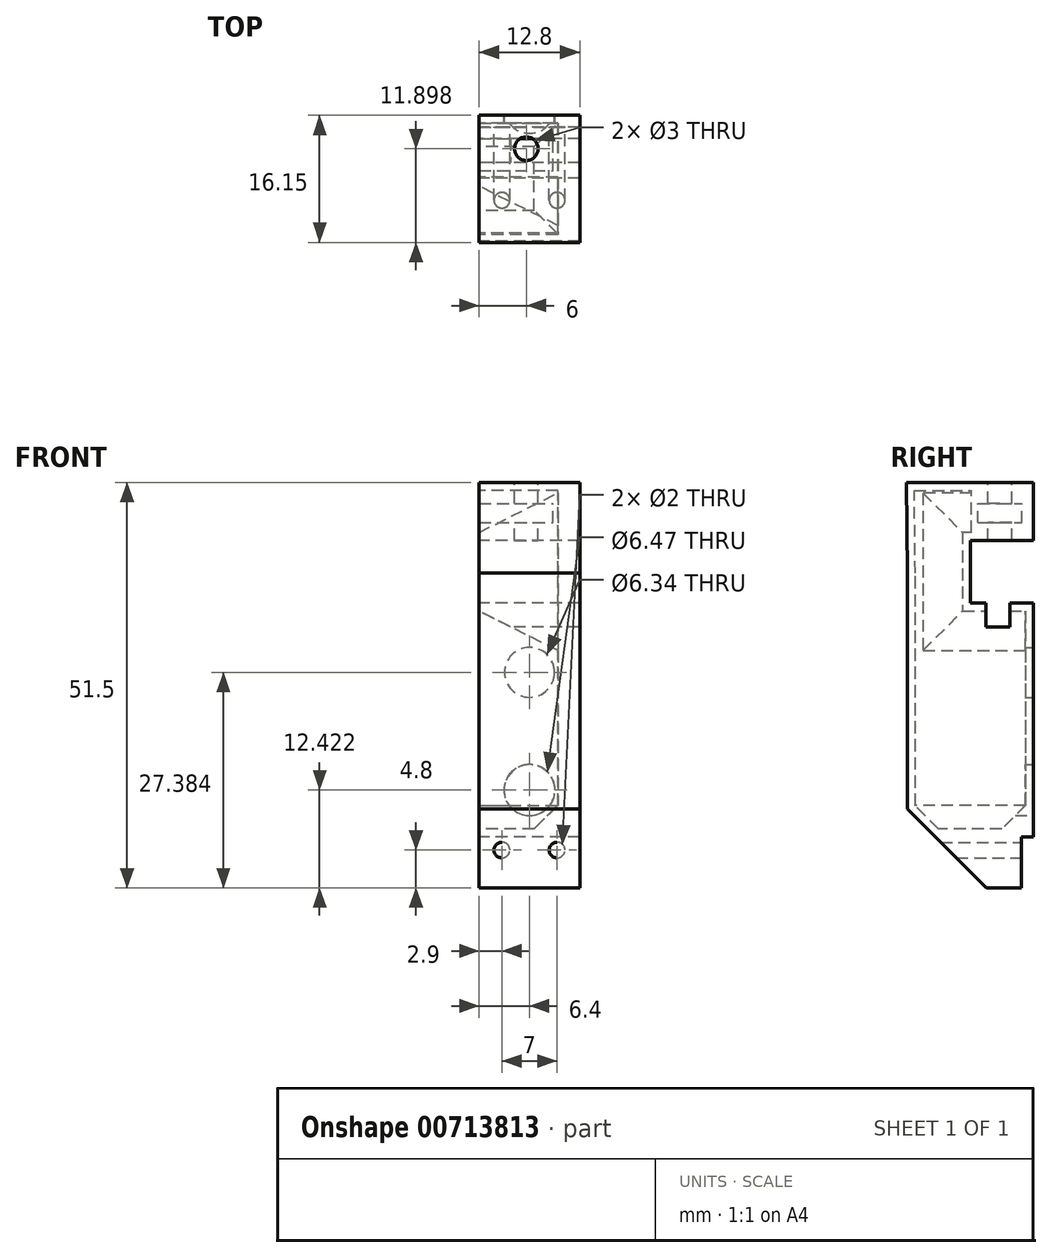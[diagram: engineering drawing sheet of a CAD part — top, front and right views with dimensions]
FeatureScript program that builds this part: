
annotation { "Feature Type Name" : "Feature", "Feature Type Description" : "" }
export const myFeature = defineFeature(function(context is Context, id is Id, definition is map)
    precondition{}
    {
        {
            var Q0;
            Q0=qCreatedBy(makeId("Right.planeOp"),FACE);
            var sketch = newSketch(context, id + "F0", { "sketchPlane" : qUnion([Q0])});
            skLineSegment(sketch, "E0.bottom", {"start": v(0, 4.16) * mm, "end": v(-8, 4.16) * mm});
            skLineSegment(sketch, "E0.top", {"start": v(0, -3.84) * mm, "end": v(-8, -3.84) * mm});
            skLineSegment(sketch, "E0.left", {"start": v(0, 4.16) * mm, "end": v(0, -3.84) * mm});
            skLineSegment(sketch, "E0.right", {"start": v(-8, 4.16) * mm, "end": v(-8, -3.84) * mm});
            skLineSegment(sketch, "E1.bottom", {"start": v(-16, 0) * mm, "end": v(0, 0) * mm});
            skLineSegment(sketch, "E1.top", {"start": v(-16, -40) * mm, "end": v(0, -40) * mm});
            skLineSegment(sketch, "E1.left", {"start": v(-16, 0) * mm, "end": v(-16, -40) * mm});
            skLineSegment(sketch, "E1.right", {"start": v(0, 0) * mm, "end": v(0, -40) * mm});
            skLineSegment(sketch, "E2", {"start": v(0, 4.16) * mm, "end": v(0, 8.64) * mm});
            skLineSegment(sketch, "E3", {"start": v(0, 8.64) * mm, "end": v(0, 11.5) * mm});
            skLineSegment(sketch, "E4", {"start": v(0, 11.5) * mm, "end": v(-16.15, 11.5) * mm});
            skLineSegment(sketch, "E5", {"start": v(-16.15, 11.5) * mm, "end": v(-16, 0) * mm});
            skLineSegment(sketch, "E6.bottom", {"start": v(-1.5, -40) * mm, "end": v(0, -40) * mm});
            skLineSegment(sketch, "E6.top", {"start": v(-1.5, -33.5) * mm, "end": v(0, -33.5) * mm});
            skLineSegment(sketch, "E6.left", {"start": v(-1.5, -40) * mm, "end": v(-1.5, -33.5) * mm});
            skLineSegment(sketch, "E6.right", {"start": v(0, -40) * mm, "end": v(0, -33.5) * mm});
            skLineSegment(sketch, "E7.bottom", {"start": v(-7.04, 6.4) * mm, "end": v(-1.49, 6.4) * mm});
            skLineSegment(sketch, "E7.top", {"start": v(-7.04, 8.85) * mm, "end": v(-1.49, 8.85) * mm});
            skLineSegment(sketch, "E7.left", {"start": v(-7.04, 6.4) * mm, "end": v(-7.04, 8.85) * mm});
            skLineSegment(sketch, "E7.right", {"start": v(-1.49, 6.4) * mm, "end": v(-1.49, 8.85) * mm});
            skLineSegment(sketch, "E8.bottom", {"start": v(-6, -3.84) * mm, "end": v(-3, -3.84) * mm});
            skLineSegment(sketch, "E8.top", {"start": v(-6, -6.85) * mm, "end": v(-3, -6.85) * mm});
            skLineSegment(sketch, "E8.left", {"start": v(-6, -3.84) * mm, "end": v(-6, -6.85) * mm});
            skLineSegment(sketch, "E8.right", {"start": v(-3, -3.84) * mm, "end": v(-3, -6.85) * mm});
            skSolve(sketch);
        }
        {
            var Q0;
            {var subQ5=sQuery(id+"F0.wireOp",EDGE,"E0.top");Q0=makeQuery(id+"F0.imprint","IMPRINT",FACE,{"disambiguationData":[TD([[makeQuery(id+"F0.imprint","IMPRINT",EDGE,{"derivedFrom":subQ5}),1.0]])]});}
            var Q1;
            {var subQ0=sQuery(id+"F0.wireOp",EDGE,"E0.bottom");Q1=makeQuery(id+"F0.imprint","IMPRINT",FACE,{"disambiguationData":[TD([[makeQuery(id+"F0.imprint","IMPRINT",EDGE,{"derivedFrom":subQ0}),-1.0]])]});}
            var Q2;
            Q2=makeQuery(id+"F0.imprint","IMPRINT",FACE,{"disambiguationData":[TD([[makeQuery(id+"F0.imprint","IMPRINT",EDGE,{"derivedFrom":sQuery(id+"F0.wireOp",EDGE,"E7.bottom")}),1.0]])]});
            extrude(context, id + "F1", {"entities" : qUnion([Q0, Q1, Q2]), "endBound" : BoundingType.SYMMETRIC, "depth" : 12.8 * mm, "offsetDistance" : 25 * mm});
        }
        {
            var Q0;
            Q0=makeQuery(id+"F1.opExtrude","SWEPT_FACE",FACE,{"disambiguationData":[OSD([sQuery(id+"F0.wireOp",EDGE,"E4")])]});
            var sketch = newSketch(context, id + "F2", { "sketchPlane" : qUnion([Q0])});
            skCircle(sketch, "E9", {"center": v(-0.4, -4.25) * mm, "radius": 1.5 * mm});
            skSolve(sketch);
        }
        {
            var Q0;
            Q0=makeQuery(id+"F0.imprint","IMPRINT",FACE,{"disambiguationData":[TD([[makeQuery(id+"F0.imprint","IMPRINT",EDGE,{"derivedFrom":sQuery(id+"F0.wireOp",EDGE,"E7.bottom")}),1.0]])]});
            extrude(context, id + "F3", {"entities" : qUnion([Q0]), "operationType" : NewBodyOperationType.REMOVE, "oppositeDirection" : true, "depth" : 9.3 * mm, "offsetDistance" : 25 * mm});
        }
        {
            var Q0;
            Q0=makeQuery(id+"F2.imprint","IMPRINT",FACE,{"disambiguationData":[TD([[makeQuery(id+"F2.imprint","IMPRINT",EDGE,{"derivedFrom":sQuery(id+"F2.wireOp",EDGE,"E9")}),1.0]])]});
            var Q1;
            Q1=sQuery(id+"F2.wireOp",EDGE,"E9");
            extrude(context, id + "F4", {"entities" : qUnion([Q0]), "operationType" : NewBodyOperationType.REMOVE, "surfaceEntities" : qUnion([Q1]), "oppositeDirection" : true, "depth" : 11.8 * mm, "offsetDistance" : 25 * mm});
        }
        {
            var Q0;
            Q0=makeQuery(id+"F0.imprint","IMPRINT",FACE,{"disambiguationData":[TD([[makeQuery(id+"F0.imprint","IMPRINT",EDGE,{"derivedFrom":sQuery(id+"F0.wireOp",EDGE,"E7.bottom")}),1.0]])]});
            extrude(context, id + "F5", {"entities" : qUnion([Q0]), "operationType" : NewBodyOperationType.REMOVE, "depth" : 3 * mm, "offsetDistance" : 25 * mm});
        }
        {
            var Q0;
            Q0=makeQuery(id+"F1.opExtrude","SWEPT_EDGE",EDGE,{"disambiguationData":[OSD([sQuery(id+"F0.wireOp",EDGE,"E1.top"),sQuery(id+"F0.wireOp",EDGE,"E1.left")])]});
            chamfer(context, id + "F6", {"entities" : qUnion([Q0]), "width" : 10 * mm, "tangentPropagation" : true});
        }
        {
            var Q0;
            Q0=makeQuery(id+"F1.opExtrude","CAP_FACE",FACE,{"disambiguationData":[OSD([sQuery(id+"F0.wireOp",EDGE,"E0.bottom"),sQuery(id+"F0.wireOp",EDGE,"E0.top"),sQuery(id+"F0.wireOp",EDGE,"E0.right"),sQuery(id+"F0.wireOp",EDGE,"E1.top"),sQuery(id+"F0.wireOp",EDGE,"E1.left"),sQuery(id+"F0.wireOp",EDGE,"E1.right"),sQuery(id+"F0.wireOp",EDGE,"E2"),sQuery(id+"F0.wireOp",EDGE,"E3"),sQuery(id+"F0.wireOp",EDGE,"E4"),sQuery(id+"F0.wireOp",EDGE,"E5"),sQuery(id+"F0.wireOp",EDGE,"E6.top"),sQuery(id+"F0.wireOp",EDGE,"E6.left")])],"isStart":true});
            var sketch = newSketch(context, id + "F7", { "sketchPlane" : qUnion([Q0])});
            skLineSegment(sketch, "E10.0.0", {"start": v(1.5, -40) * mm, "end": v(6, -40) * mm});
            skLineSegment(sketch, "E10.0.1", {"start": v(6, -40) * mm, "end": v(16, -30) * mm});
            skLineSegment(sketch, "E10.0.2", {"start": v(16, -30) * mm, "end": v(16, 0) * mm});
            skLineSegment(sketch, "E10.0.3", {"start": v(16, 0) * mm, "end": v(16.15, 11.5) * mm});
            skLineSegment(sketch, "E10.0.4", {"start": v(16.15, 11.5) * mm, "end": v(0, 11.5) * mm});
            skLineSegment(sketch, "E10.0.5", {"start": v(0, 11.5) * mm, "end": v(0, 4.16) * mm});
            skLineSegment(sketch, "E10.0.6", {"start": v(0, 4.16) * mm, "end": v(8, 4.16) * mm});
            skLineSegment(sketch, "E10.0.7", {"start": v(8, 4.16) * mm, "end": v(8, -3.84) * mm});
            skLineSegment(sketch, "E10.0.8", {"start": v(8, -3.84) * mm, "end": v(0, -3.84) * mm});
            skLineSegment(sketch, "E10.0.9", {"start": v(0, -3.84) * mm, "end": v(0, -33.5) * mm});
            skLineSegment(sketch, "E10.0.10", {"start": v(0, -33.5) * mm, "end": v(1.5, -33.5) * mm});
            skLineSegment(sketch, "E10.0.11", {"start": v(1.5, -33.5) * mm, "end": v(1.5, -40) * mm});
            skLineSegment(sketch, "E11.0", {"start": v(15, 0) * mm, "end": v(15.14, 10.5) * mm});
            skLineSegment(sketch, "E11.1", {"start": v(9, -4.84) * mm, "end": v(1, -4.84) * mm});
            skLineSegment(sketch, "E11.2", {"start": v(9, 5.16) * mm, "end": v(9, -4.84) * mm});
            skLineSegment(sketch, "E11.3", {"start": v(1, 5.16) * mm, "end": v(9, 5.16) * mm});
            skLineSegment(sketch, "E11.4", {"start": v(1, 10.5) * mm, "end": v(1, 5.16) * mm});
            skLineSegment(sketch, "E11.5", {"start": v(1, -4.84) * mm, "end": v(1, -32.5) * mm});
            skLineSegment(sketch, "E11.6", {"start": v(15.14, 10.5) * mm, "end": v(1, 10.5) * mm});
            skLineSegment(sketch, "E11.7", {"start": v(1, -32.5) * mm, "end": v(2.5, -32.5) * mm});
            skLineSegment(sketch, "E11.8", {"start": v(2.5, -32.5) * mm, "end": v(2.5, -39) * mm});
            skLineSegment(sketch, "E11.9", {"start": v(2.5, -39) * mm, "end": v(5.59, -39) * mm});
            skLineSegment(sketch, "E11.10", {"start": v(5.59, -39) * mm, "end": v(15, -29.59) * mm});
            skLineSegment(sketch, "E11.11", {"start": v(15, -29.59) * mm, "end": v(15, 0) * mm});
            skLineSegment(sketch, "E12", {"start": v(7.85, 5.16) * mm, "end": v(7.85, 10.5) * mm});
            skLineSegment(sketch, "E13", {"start": v(1, -21.14) * mm, "end": v(1, -14.36) * mm});
            skLineSegment(sketch, "E14", {"start": v(2.5, -32.5) * mm, "end": v(12.09, -32.5) * mm});
            skSolve(sketch);
        }
        {
            var Q0;
            Q0=makeQuery(id+"F1.opExtrude","CAP_FACE",FACE,{"disambiguationData":[OSD([sQuery(id+"F0.wireOp",EDGE,"E0.bottom"),sQuery(id+"F0.wireOp",EDGE,"E0.top"),sQuery(id+"F0.wireOp",EDGE,"E0.right"),sQuery(id+"F0.wireOp",EDGE,"E1.top"),sQuery(id+"F0.wireOp",EDGE,"E1.left"),sQuery(id+"F0.wireOp",EDGE,"E1.right"),sQuery(id+"F0.wireOp",EDGE,"E2"),sQuery(id+"F0.wireOp",EDGE,"E3"),sQuery(id+"F0.wireOp",EDGE,"E4"),sQuery(id+"F0.wireOp",EDGE,"E5"),sQuery(id+"F0.wireOp",EDGE,"E6.top"),sQuery(id+"F0.wireOp",EDGE,"E6.left")])],"isStart":false});
            var sketch = newSketch(context, id + "F8", { "sketchPlane" : qUnion([Q0])});
            skLineSegment(sketch, "E15.0", {"start": v(-14.32, 9.7) * mm, "end": v(-14.2, 0.01) * mm});
            skLineSegment(sketch, "E15.1", {"start": v(-3.3, -31.7) * mm, "end": v(-1.8, -31.7) * mm});
            skLineSegment(sketch, "E15.2", {"start": v(-3.3, -38.2) * mm, "end": v(-3.3, -31.7) * mm});
            skLineSegment(sketch, "E15.3", {"start": v(-5.25, -38.2) * mm, "end": v(-3.3, -38.2) * mm});
            skLineSegment(sketch, "E15.4", {"start": v(-14.2, -29.25) * mm, "end": v(-5.25, -38.2) * mm});
            skLineSegment(sketch, "E15.5", {"start": v(-1.8, -31.7) * mm, "end": v(-1.8, -5.64) * mm});
            skLineSegment(sketch, "E15.6", {"start": v(-14.2, 0.01) * mm, "end": v(-14.2, -29.25) * mm});
            skLineSegment(sketch, "E15.7", {"start": v(-1.8, -5.64) * mm, "end": v(-9.8, -5.64) * mm});
            skLineSegment(sketch, "E15.8", {"start": v(-9.8, -5.64) * mm, "end": v(-9.8, 5.96) * mm});
            skLineSegment(sketch, "E15.9", {"start": v(-9.8, 5.96) * mm, "end": v(-1.8, 5.96) * mm});
            skLineSegment(sketch, "E15.10", {"start": v(-1.8, 5.96) * mm, "end": v(-1.8, 9.7) * mm});
            skLineSegment(sketch, "E15.11", {"start": v(-1.8, 9.7) * mm, "end": v(-14.32, 9.7) * mm});
            skSolve(sketch);
        }
        {
            var Q0;
            Q0=makeQuery(id+"F7.imprint","IMPRINT",FACE,{"disambiguationData":[TD([[makeQuery(id+"F7.imprint","IMPRINT",EDGE,{"derivedFrom":sQuery(id+"F7.wireOp",EDGE,"E11.0")}),1.0]])]});
            var Q1;
            {var subQ0=sQuery(id+"F7.wireOp",EDGE,"W9cZQmMh-SMga-qgHw-FY0C-kd683LFS7WeK");Q1=makeQuery(id+"F7.imprint","IMPRINT",FACE,{"disambiguationData":[TD([[makeQuery(id+"F7.imprint","IMPRINT",EDGE,{"derivedFrom":subQ0}),-1.0]])]});}
            var Q2;
            {var subQ0=sQuery(id+"F7.wireOp",EDGE,"oMO8bEbg-HHsQ-YIDq-fVXH-qFGtp7pXah5B");Q2=makeQuery(id+"F7.imprint","IMPRINT",FACE,{"disambiguationData":[TD([[makeQuery(id+"F7.imprint","IMPRINT",EDGE,{"derivedFrom":subQ0}),1.0]])]});}
            var Q3;
            {var subQ0=sQuery(id+"F7.wireOp",EDGE,"1qnYtKGn-a9Li-eoZe-lueF-fTprzZPRoMs7");Q3=makeQuery(id+"F7.imprint","IMPRINT",FACE,{"disambiguationData":[TD([[makeQuery(id+"F7.imprint","IMPRINT",EDGE,{"derivedFrom":subQ0}),1.0]])]});}
            var Q4;
            {var subQ3=sQuery(id+"F7.wireOp",EDGE,"E11.7");Q4=makeQuery(id+"F7.imprint","IMPRINT",FACE,{"disambiguationData":[TD([[makeQuery(id+"F7.imprint","IMPRINT",EDGE,{"derivedFrom":subQ3}),1.0]])]});}
            var Q5;
            {var subQ0=sQuery(id+"F7.wireOp",EDGE,"xWiPD5sj-9TZn-cRoH-leyY-KUWepa9Cie01");Q5=makeQuery(id+"F7.imprint","IMPRINT",FACE,{"disambiguationData":[TD([[makeQuery(id+"F7.imprint","IMPRINT",EDGE,{"derivedFrom":subQ0}),-1.0]])]});}
            extrude(context, id + "F9", {"entities" : qUnion([Q0, Q1, Q2, Q3, Q4, Q5]), "operationType" : NewBodyOperationType.REMOVE, "oppositeDirection" : true, "depth" : 10 * mm, "offsetDistance" : 25 * mm});
        }
        {
            var Q0;
            Q0=makeQuery(id+"F1.opExtrude","SWEPT_FACE",FACE,{"disambiguationData":[OSD([sQuery(id+"F0.wireOp",EDGE,"E6.left")])]});
            var sketch = newSketch(context, id + "F10", { "sketchPlane" : qUnion([Q0])});
            skCircle(sketch, "E16", {"center": v(3.5, -35.2) * mm, "radius": 1 * mm});
            skCircle(sketch, "E17", {"center": v(-3.5, -35.2) * mm, "radius": 1 * mm});
            skSolve(sketch);
        }
        {
            var Q0;
            Q0=makeQuery(id+"F10.imprint","IMPRINT",FACE,{"disambiguationData":[TD([[makeQuery(id+"F10.imprint","IMPRINT",EDGE,{"derivedFrom":sQuery(id+"F10.wireOp",EDGE,"E17")}),1.0]])]});
            var Q1;
            Q1=makeQuery(id+"F10.imprint","IMPRINT",FACE,{"disambiguationData":[TD([[makeQuery(id+"F10.imprint","IMPRINT",EDGE,{"derivedFrom":sQuery(id+"F10.wireOp",EDGE,"E16")}),1.0]])]});
            var Q2;
            Q2=sQuery(id+"F10.wireOp",EDGE,"E16");
            var Q3;
            Q3=sQuery(id+"F10.wireOp",EDGE,"E17");
            extrude(context, id + "F11", {"entities" : qUnion([Q0, Q1]), "operationType" : NewBodyOperationType.REMOVE, "surfaceEntities" : qUnion([Q2, Q3]), "oppositeDirection" : true, "depth" : 16.7 * mm, "offsetDistance" : 25 * mm});
        }
        {
            var Q0;
            Q0=makeQuery(id+"F1.opExtrude","SWEPT_FACE",FACE,{"disambiguationData":[OSD([sQuery(id+"F0.wireOp",EDGE,"E1.right")])]});
            var sketch = newSketch(context, id + "F12", { "sketchPlane" : qUnion([Q0])});
            skCircle(sketch, "E18", {"center": v(0, -12.62) * mm, "radius": 3.17 * mm});
            skCircle(sketch, "E19", {"center": v(0, -27.58) * mm, "radius": 3.23 * mm});
            skSolve(sketch);
        }
        {
            var Q0;
            Q0=makeQuery(id+"F9.boolean.opBoolean","COPY",EDGE,{"derivedFrom":makeQuery(id+"F9.opExtrude","CAP_EDGE",EDGE,{"disambiguationData":[OSD([sQuery(id+"F7.wireOp",EDGE,"E11.7"),sQuery(id+"F7.wireOp",EDGE,"E14")])],"isStart":false})});
            var Q1;
            Q1=makeQuery(id+"F9.boolean.opBoolean","COPY",EDGE,{"derivedFrom":makeQuery(id+"F9.opExtrude","SWEPT_EDGE",EDGE,{"disambiguationData":[OSD([sQuery(id+"F7.wireOp",EDGE,"E11.5"),sQuery(id+"F7.wireOp",EDGE,"E11.7")])]})});
            chamfer(context, id + "F13", {"entities" : qUnion([Q0, Q1]), "width" : 3 * mm, "tangentPropagation" : true});
        }
        {
            var Q0;
            Q0=makeQuery(id+"F12.imprint","IMPRINT",FACE,{"disambiguationData":[TD([[makeQuery(id+"F12.imprint","IMPRINT",EDGE,{"derivedFrom":sQuery(id+"F12.wireOp",EDGE,"U1l2S5FM-SpEA-PXqX-huyP-1ljV85ucmUwr.bottom")}),-1.0]])]});
            var Q1;
            Q1=makeQuery(id+"F12.imprint","IMPRINT",FACE,{"disambiguationData":[TD([[makeQuery(id+"F12.imprint","IMPRINT",EDGE,{"derivedFrom":sQuery(id+"F12.wireOp",EDGE,"yQKHxZbq-3swJ-b0gf-90DM-MQPt5EavAIww.bottom")}),-1.0]])]});
            var Q2;
            Q2=makeQuery(id+"F12.imprint","IMPRINT",FACE,{"disambiguationData":[TD([[makeQuery(id+"F12.imprint","IMPRINT",EDGE,{"derivedFrom":sQuery(id+"F12.wireOp",EDGE,"E18")}),1.0]])]});
            var Q3;
            Q3=makeQuery(id+"F12.imprint","IMPRINT",FACE,{"disambiguationData":[TD([[makeQuery(id+"F12.imprint","IMPRINT",EDGE,{"derivedFrom":sQuery(id+"F12.wireOp",EDGE,"E19")}),1.0]])]});
            extrude(context, id + "F14", {"entities" : qUnion([Q0, Q1, Q2, Q3]), "operationType" : NewBodyOperationType.REMOVE, "oppositeDirection" : true, "depth" : 11.3 * mm, "offsetDistance" : 25 * mm});
        }
        {
            var Q0;
            {var subQ0=sQuery(id+"F7.wireOp",EDGE,"E11.1");Q0=makeQuery(id+"F9.boolean.opBoolean","COPY",EDGE,{"derivedFrom":makeQuery(id+"F9.opExtrude","CAP_EDGE",EDGE,{"disambiguationData":[OSD([subQ0]),TDD([makeQuery(id+"F7.imprint","IMPRINT",EDGE,{"disambiguationData":[TD([[makeQuery(id+"F7.imprint","INTERSECT",VERTEX,{"derivedFrom":[subQ0,sQuery(id+"F7.wireOp",EDGE,"E11.2")]}),-1.0]])],"derivedFrom":subQ0})])],"isStart":false})});}
            var Q1;
            Q1=makeQuery(id+"F9.boolean.opBoolean","COPY",EDGE,{"derivedFrom":makeQuery(id+"F9.opExtrude","CAP_EDGE",EDGE,{"disambiguationData":[OSD([sQuery(id+"F7.wireOp",EDGE,"E11.2")])],"isStart":false})});
            var Q2;
            Q2=makeQuery(id+"F9.boolean.opBoolean","COPY",EDGE,{"derivedFrom":makeQuery(id+"F9.opExtrude","CAP_EDGE",EDGE,{"disambiguationData":[OSD([sQuery(id+"F7.wireOp",EDGE,"E11.3")])],"isStart":false})});
            chamfer(context, id + "F15", {"entities" : qUnion([Q0, Q1, Q2]), "chamferType" : ChamferType.TWO_OFFSETS, "width1" : 5 * mm, "oppositeDirection" : false, "width2" : 10 * mm, "tangentPropagation" : true});
        }
    });
